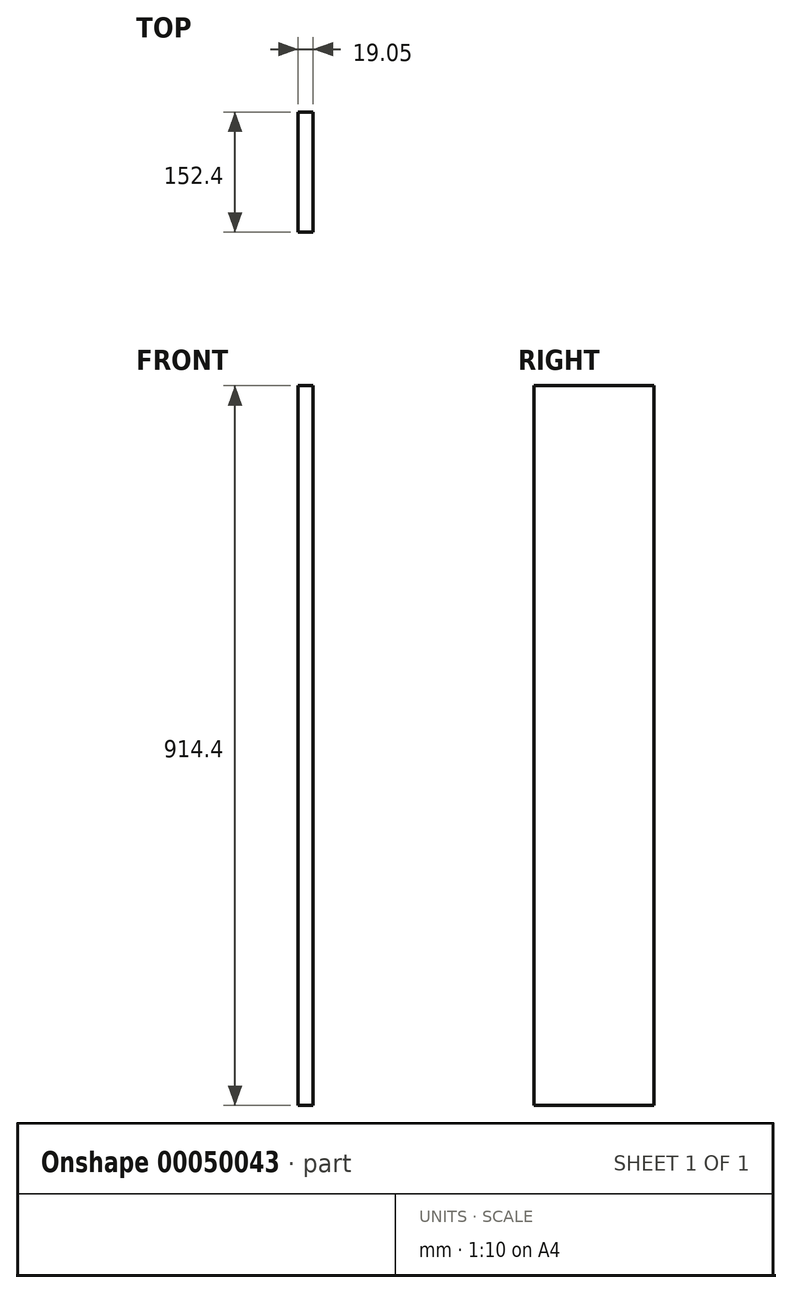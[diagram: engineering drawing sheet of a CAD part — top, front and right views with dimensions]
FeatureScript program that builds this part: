
annotation { "Feature Type Name" : "Feature", "Feature Type Description" : "" }
export const myFeature = defineFeature(function(context is Context, id is Id, definition is map)
    precondition{}
    {
        {
            var Q0;
            Q0=qCreatedBy(makeId("Right.planeOp"),FACE);
            var sketch = newSketch(context, id + "F0", { "sketchPlane" : qUnion([Q0])});
            skLineSegment(sketch, "E0.bottom", {"start": v(0, 0) * mm, "end": v(152.4, 0) * mm});
            skLineSegment(sketch, "E0.top", {"start": v(0, 914.4) * mm, "end": v(152.4, 914.4) * mm});
            skLineSegment(sketch, "E0.left", {"start": v(0, 0) * mm, "end": v(0, 914.4) * mm});
            skLineSegment(sketch, "E0.right", {"start": v(152.4, 0) * mm, "end": v(152.4, 914.4) * mm});
            skSolve(sketch);
        }
        {
            var Q0;
            Q0=makeQuery(id+"F0.imprint","IMPRINT",FACE,{"disambiguationData":[TD([[makeQuery(id+"F0.imprint","IMPRINT",EDGE,{"derivedFrom":sQuery(id+"F0.wireOp",EDGE,"E0.bottom")}),1.0]])]});
            extrude(context, id + "F1", {"entities" : qUnion([Q0]), "depth" : 19.05 * mm});
        }
    });
